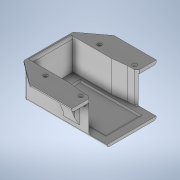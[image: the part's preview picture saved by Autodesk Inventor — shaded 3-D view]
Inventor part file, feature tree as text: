
AUTODESK INVENTOR PART (.ipt)
format: ipt  version: 2022.6 (Build 266554000, 554)  size: 412,160 bytes
history: native  units: mm
features: sketch x11, projected_geometry x11, extrude x9, chamfer x5, fillet x5, plane x4, hole x1, rib x1, mirror x1
ambient origin geometry x8: Origin, YZ Plane, XZ Plane, XY Plane, X Axis, Y Axis, Z Axis, Center Point
bodies: Solid1 (feature_tree)
feature tree (48):
  extrude  "Extrusion1"  Depth=36.0mm
  extrude  "Extrusion2"  Depth=3.0mm
  extrude  "Extrusion4"  Depth=3.0mm
  hole  "Hole1"  [1 undecoded]
  plane  "Work Plane1"
  rib  "Rib1"
  plane  "Work Plane2"
  chamfer  "Chamfer2"  Distance=3.0mm
  mirror  "Mirror2"
  chamfer  "Chamfer3"  Distance=40.5mm
  fillet  "Fillet3"  Radius=5.0mm
  fillet  "Fillet5"  Radius=17.0mm
  fillet  "Fillet6"  Radius=2.0mm
  extrude  "Extrusion5"  Depth=2.0mm TaperAngle=45.0deg
  fillet  "Fillet7"  Radius=2.0mm
  plane  "Work Plane3"
  extrude  "Extrusion6"  Depth=2.0mm
  extrude  "Extrusion8"  Depth=2.0mm
  chamfer  "Chamfer4"  Distance=18.0mm
  extrude  "Extrusion10"  Depth=5.0mm
  chamfer  "Chamfer5"  Distance=35.0mm
  fillet  "Fillet9"  Radius=0.4mm
  plane  "Work Plane4"
  extrude  "Extrusion11"  Depth=2.0mm
  chamfer  "Chamfer6"  Distance=10.0mm
  extrude  "Extrusion12"  Depth=2.0mm TaperAngle=0.0deg
  sketch  "Sketch1"  dims[d0=36.0mm d1=78.0mm]
  sketch  "Sketch2"  dims[d2=2.5mm d3=0.0mm d4=3.0mm]
  sketch  "Sketch3"  dims[d5=3.0mm d6=3.0mm]
  sketch  "Sketch4"  dims[d7=26.5mm d8=2.5mm d9=0.0mm d10=0.0mm d30=15.0mm]
  sketch  "Sketch5"  dims[d31=15.0mm]
  projected_geometry  "Projected Loop1"
  projected_geometry  "Projected Loop2"
  projected_geometry  "Projected Loop3"
  sketch  "Sketch6"  dims[d32=20.0mm d33=3.0mm d34=0.0mm]
  projected_geometry  "Projected Loop4"
  sketch  "Sketch7"  dims[d43=30.0mm]
  projected_geometry  "Projected Loop5"
  projected_geometry  "Projected Loop7"
  projected_geometry  "Projected Loop8"
  sketch  "Sketch9"  dims[d45=20.5mm]
  projected_geometry  "Projected Loop11"
  sketch  "Sketch11"  dims[d47=3.4mm d48=6.0mm d49=4.0mm d50=2.0mm d51=90.0deg d52=8.0mm d53=20.594885mm]
  projected_geometry  "Projected Loop12"
  sketch  "Sketch12"  dims[d56=5.0mm]
  sketch  "Sketch14"  dims[d57=5.0mm d58=40.5mm d60=5.0mm d61=1.0mm d62=10.0mm d63=0.0mm d64=0.0mm d65=1.0mm d66=1.0mm d67=17.0mm d68=2.0mm d69=2.0mm d70=45.0deg d71=2.0mm d72=2.0mm d73=45.0deg d76=2.0mm d78=2.0mm d79=2.0mm d80=18.0mm d81=25.0mm d82=35.0mm d83=0.4mm d84=0.0mm d85=2.0mm d88=10.0mm d89=0.0mm d90=2.0mm d91=0.0mm d96=25.0mm d97=0.0mm d98=0.0mm d99=3.0mm d100=2.0mm d101=45.0deg d106=3.0mm d107=2.5mm d108=1.0mm d109=0.5mm d110=10.0mm d111=3.0mm d112=1.5mm d114=8.0mm d115=20.0mm d116=10.0mm d117=0.0mm d119=2.0mm d120=2.0mm d121=45.0deg d122=1.0mm d123=18.0mm d124=0.8mm d125=28.0mm d126=50.0mm d127=0.0mm d128=1.5mm d129=0.8mm d130=45.0deg d131=5.4mm d132=5.0mm d133=0.0mm d35=0.5mm d36=0.872665mm d77=0.0mm]
  projected_geometry  "Projected Loop13"
  projected_geometry  "Projected Loop14"
note: 1 required parameter value undecoded (feature->parameter linkage not recoverable at this tier; creation-order binding heuristic only, values carry confidence <= 0.55)
